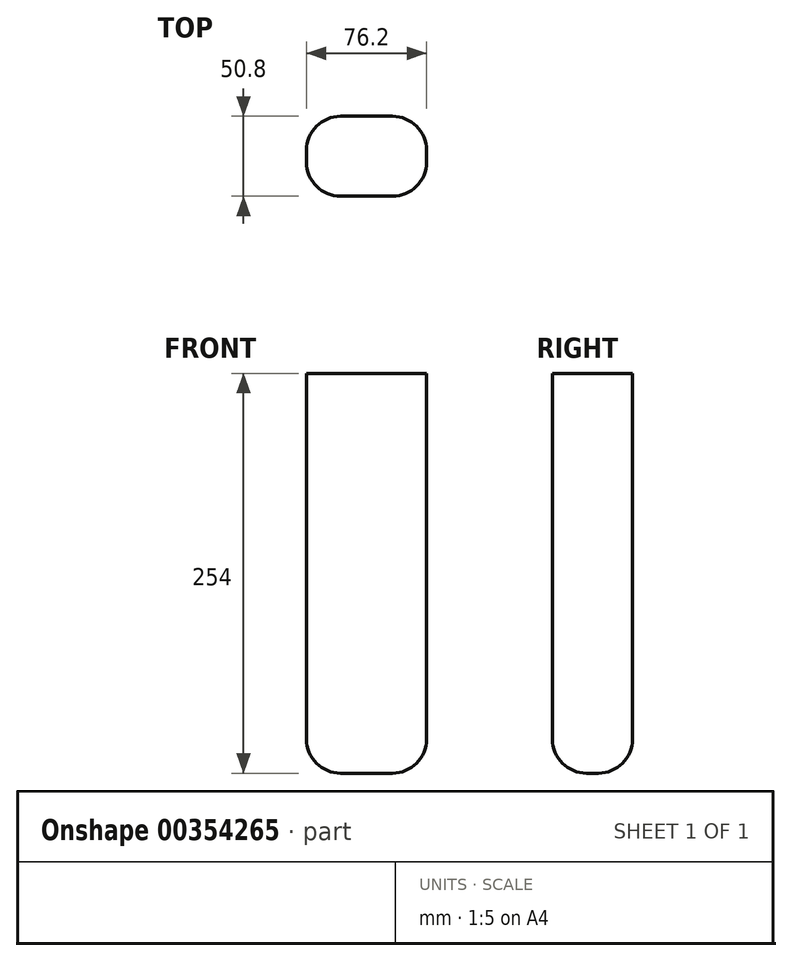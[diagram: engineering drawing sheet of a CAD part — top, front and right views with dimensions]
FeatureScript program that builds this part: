
annotation { "Feature Type Name" : "Feature", "Feature Type Description" : "" }
export const myFeature = defineFeature(function(context is Context, id is Id, definition is map)
    precondition{}
    {
        {
            var Q0;
            Q0=qCreatedBy(makeId("Top.planeOp"),FACE);
            var sketch = newSketch(context, id + "F0", { "sketchPlane" : qUnion([Q0])});
            skLineSegment(sketch, "E0", {"start": v(-29.27, -42.05) * mm, "end": v(-29.27, 8.75) * mm});
            skLineSegment(sketch, "E1", {"start": v(-29.27, 8.75) * mm, "end": v(46.93, 8.75) * mm});
            skLineSegment(sketch, "E2", {"start": v(46.93, 8.75) * mm, "end": v(46.93, -42.05) * mm});
            skLineSegment(sketch, "E3", {"start": v(46.93, -42.05) * mm, "end": v(-29.27, -42.05) * mm});
            skSolve(sketch);
        }
        {
            var Q0;
            Q0=makeQuery(id+"F0.imprint","IMPRINT",FACE,{"disambiguationData":[TD([[makeQuery(id+"F0.imprint","IMPRINT",EDGE,{"derivedFrom":sQuery(id+"F0.wireOp",EDGE,"E0")}),-1.0]])]});
            extrude(context, id + "F1", {"entities" : qUnion([Q0]), "endBound" : BoundingType.SYMMETRIC, "depth" : 254 * mm});
        }
        {
            var Q0;
            Q0=makeQuery(id+"F1.opExtrude","CAP_EDGE",EDGE,{"disambiguationData":[OSD([sQuery(id+"F0.wireOp",EDGE,"E3")])],"isStart":true});
            var Q1;
            Q1=makeQuery(id+"F1.opExtrude","CAP_EDGE",EDGE,{"disambiguationData":[OSD([sQuery(id+"F0.wireOp",EDGE,"E1")])],"isStart":true});
            var Q2;
            Q2=makeQuery(id+"F1.opExtrude","CAP_EDGE",EDGE,{"disambiguationData":[OSD([sQuery(id+"F0.wireOp",EDGE,"E2")])],"isStart":true});
            var Q3;
            Q3=makeQuery(id+"F1.opExtrude","CAP_EDGE",EDGE,{"disambiguationData":[OSD([sQuery(id+"F0.wireOp",EDGE,"E0")])],"isStart":true});
            var Q4;
            Q4=makeQuery(id+"F1.opExtrude","SWEPT_EDGE",EDGE,{"disambiguationData":[OSD([sQuery(id+"F0.wireOp",EDGE,"E0"),sQuery(id+"F0.wireOp",EDGE,"E1")])]});
            var Q5;
            Q5=makeQuery(id+"F1.opExtrude","SWEPT_EDGE",EDGE,{"disambiguationData":[OSD([sQuery(id+"F0.wireOp",EDGE,"E0"),sQuery(id+"F0.wireOp",EDGE,"E3")])]});
            var Q6;
            Q6=makeQuery(id+"F1.opExtrude","SWEPT_EDGE",EDGE,{"disambiguationData":[OSD([sQuery(id+"F0.wireOp",EDGE,"E2"),sQuery(id+"F0.wireOp",EDGE,"E3")])]});
            var Q7;
            Q7=makeQuery(id+"F1.opExtrude","SWEPT_EDGE",EDGE,{"disambiguationData":[OSD([sQuery(id+"F0.wireOp",EDGE,"E1"),sQuery(id+"F0.wireOp",EDGE,"E2")])]});
            fillet(context, id + "F2", {"entities" : qUnion([Q0, Q1, Q2, Q3, Q4, Q5, Q6, Q7]), "radius" : 21.59 * mm, "tangentPropagation" : true, "allowEdgeOverflow" : false});
        }
    });
